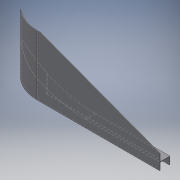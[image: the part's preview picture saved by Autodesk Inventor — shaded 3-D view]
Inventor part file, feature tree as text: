
AUTODESK INVENTOR PART (.ipt)
format: ipt  version: 2018 (Build 220112000, 112)  size: 175,616 bytes
history: native  units: mm
features: extrude x6, sketch x6, other x1, projected_geometry x1
ambient origin geometry x8: Origin, YZ Plane, XZ Plane, XY Plane, X Axis, Y Axis, Z Axis, Center Point
bodies: Body1 (feature_tree)
feature tree (14):
  extrude  "押し出し1"  Depth=250.0mm
  extrude  "押し出し2"  Depth=500.0mm
  extrude  "押し出し5"  Depth=100.0mm
  extrude  "押し出し7"  Depth=200.0mm
  other  "面を削除1"
  extrude  "押し出し8"  Depth=35.0mm TaperAngle=0.0deg
  extrude  "押し出し9"  Depth=90.0mm
  sketch  "スケッチ1"
  sketch  "スケッチ2"
  sketch  "スケッチ5"
  sketch  "スケッチ8"
  sketch  "スケッチ9"
  projected_geometry  "投影ループ1"
  sketch  "スケッチ10"
